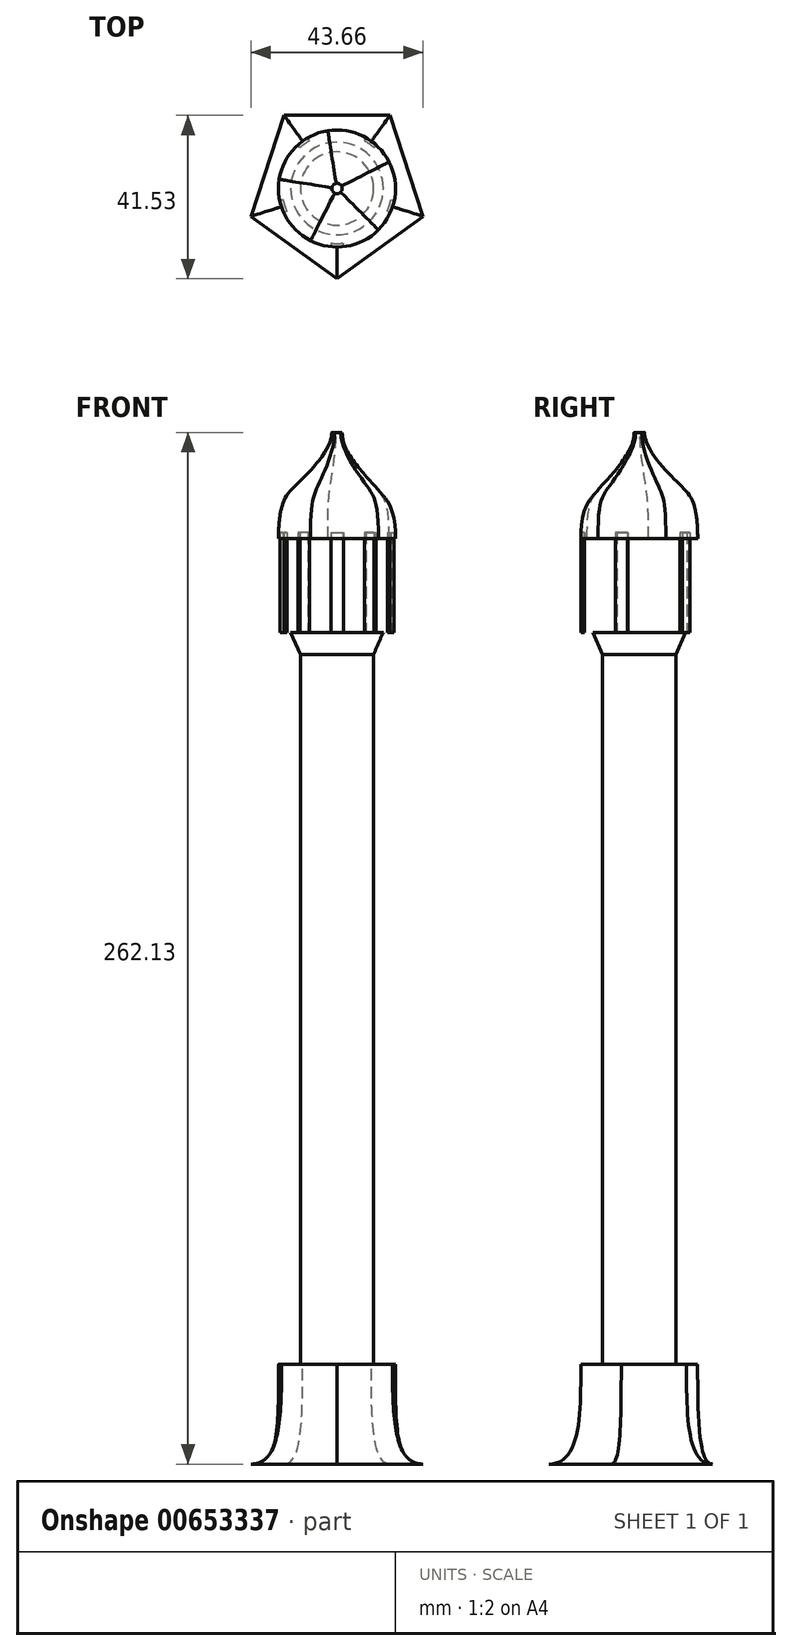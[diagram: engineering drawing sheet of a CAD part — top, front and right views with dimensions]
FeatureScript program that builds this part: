
annotation { "Feature Type Name" : "Feature", "Feature Type Description" : "" }
export const myFeature = defineFeature(function(context is Context, id is Id, definition is map)
    precondition{}
    {
        {
            var Q0;
            Q0=qCreatedBy(makeId("Top.planeOp"),FACE);
            var sketch = newSketch(context, id + "F0", { "sketchPlane" : qUnion([Q0])});
            skCircle(sketch, "E0.cCircle", {"center": v(0, 0) * mm, "radius": 18.57 * mm, "construction": true});
            skLineSegment(sketch, "E0.0", {"start": v(-13.5, 18.57) * mm, "end": v(13.5, 18.57) * mm});
            skLineSegment(sketch, "E0.1", {"start": v(13.5, 18.57) * mm, "end": v(21.83, -7.1) * mm});
            skLineSegment(sketch, "E0.2", {"start": v(21.83, -7.1) * mm, "end": v(0, -22.96) * mm});
            skLineSegment(sketch, "E0.3", {"start": v(0, -22.96) * mm, "end": v(-21.83, -7.1) * mm});
            skLineSegment(sketch, "E0.4", {"start": v(-21.83, -7.1) * mm, "end": v(-13.5, 18.57) * mm});
            skPoint(sketch, "E0.0.midPoint", {"position": v(0, 18.57) * mm});
            skSolve(sketch);
        }
        {
            var Q0;
            Q0=qCreatedBy(makeId("Top.planeOp"),FACE);
            cPlane(context, id + "F1", {"entities" : qUnion([Q0]), "cplaneType" : CPlaneType.OFFSET, "offset" : 25.4 * mm, "width" : 152.4 * mm, "height" : 152.4 * mm});
        }
        {
            var Q0;
            Q0=qCreatedBy(id+"F1.planeOp",FACE);
            var sketch = newSketch(context, id + "F2", { "sketchPlane" : qUnion([Q0])});
            skCircle(sketch, "E1", {"center": v(0, 0) * mm, "radius": 14.84 * mm});
            skSolve(sketch);
        }
        {
            var Q0;
            Q0 = qSketchRegion(id + "F0", true);
            var Q1;
            Q1 = qSketchRegion(id + "F2", true);
            loft(context, id + "F3", {"startCondition" : LoftEndDerivativeType.TANGENT_TO_PROFILE, "startMagnitude" : 3, "endCondition" : LoftEndDerivativeType.TANGENT_TO_PROFILE, "endMagnitude" : 0, "sheetProfilesArray" : [{ "sheetProfileEntities" : qUnion([Q0]) }, { "sheetProfileEntities" : qUnion([Q1]) }]});
        }
        {
            var Q0;
            Q0=makeQuery(id+"F3.opLoft","CAP_FACE",FACE,{"disambiguationData":[OSD([makeQuery(id+"F2.imprint","IMPRINT",FACE,{"disambiguationData":[TD([[makeQuery(id+"F2.imprint","IMPRINT",EDGE,{"derivedFrom":sQuery(id+"F2.wireOp",EDGE,"E1")}),1.0]])]})])],"isStart":true});
            var sketch = newSketch(context, id + "F4", { "sketchPlane" : qUnion([Q0])});
            skCircle(sketch, "E2", {"center": v(0, 0) * mm, "radius": 9.3 * mm});
            skSolve(sketch);
        }
        {
            var Q0;
            Q0 = qSketchRegion(id + "F4", true);
            extrude(context, id + "F5", {"entities" : qUnion([Q0]), "operationType" : NewBodyOperationType.ADD, "depth" : 180.34 * mm, "offsetDistance" : 25.4 * mm});
        }
        {
            var Q0;
            Q0=makeQuery(id+"F5.opExtrude","CAP_FACE",FACE,{"disambiguationData":[OSD([sQuery(id+"F4.wireOp",EDGE,"E2")])],"isStart":false});
            cPlane(context, id + "F6", {"entities" : qUnion([Q0]), "cplaneType" : CPlaneType.OFFSET, "offset" : 5.6 * mm, "width" : 152.4 * mm, "height" : 152.4 * mm});
        }
        {
            var Q0;
            Q0=qCreatedBy(id+"F6.planeOp",FACE);
            var sketch = newSketch(context, id + "F7", { "sketchPlane" : qUnion([Q0])});
            skCircle(sketch, "E3", {"center": v(0, 0) * mm, "radius": 11.76 * mm});
            skSolve(sketch);
        }
        {
            var Q1;
            Q1=makeQuery(id+"F7.imprint","IMPRINT",FACE,{"disambiguationData":[TD([[makeQuery(id+"F7.imprint","IMPRINT",EDGE,{"derivedFrom":sQuery(id+"F7.wireOp",EDGE,"E3")}),1.0]])]});
            var Q2;
            Q2=makeQuery(id+"F5.opExtrude","CAP_FACE",FACE,{"disambiguationData":[OSD([sQuery(id+"F4.wireOp",EDGE,"E2")])],"isStart":false});
            loft(context, id + "F8", {"operationType" : NewBodyOperationType.ADD, "sheetProfilesArray" : [{ "sheetProfileEntities" : qUnion([Q1]) }, { "sheetProfileEntities" : qUnion([Q2]) }]});
        }
        {
            var Q0;
            Q0=makeQuery(id+"F8.opLoft","CAP_FACE",FACE,{"disambiguationData":[OSD([makeQuery(id+"F7.imprint","IMPRINT",FACE,{"disambiguationData":[TD([[makeQuery(id+"F7.imprint","IMPRINT",EDGE,{"derivedFrom":sQuery(id+"F7.wireOp",EDGE,"E3")}),1.0]])]})])],"isStart":true});
            var sketch = newSketch(context, id + "F9", { "sketchPlane" : qUnion([Q0])});
            skArc(sketch, "E4", {"start": v(-6.97, 12.13) * mm, "mid": v(-8.24, 11.3) * mm, "end": v(-9.4, 10.36) * mm});
            skArc(sketch, "E5", {"start": v(-7.38, 12.83) * mm, "mid": v(-8.71, 11.96) * mm, "end": v(-9.95, 10.96) * mm});
            skLineSegment(sketch, "E6", {"start": v(6.95, 12.14) * mm, "end": v(7.35, 12.85) * mm});
            skLineSegment(sketch, "E7", {"start": v(9.38, 10.38) * mm, "end": v(9.92, 10.98) * mm});
            skLineSegment(sketch, "E8.1.0", {"start": v(-6.97, 12.13) * mm, "end": v(-7.38, 12.83) * mm});
            skLineSegment(sketch, "E8.1.1", {"start": v(-9.4, 10.36) * mm, "end": v(-9.95, 10.96) * mm});
            skLineSegment(sketch, "E8.2.0", {"start": v(-13.69, -2.89) * mm, "end": v(-14.48, -3.05) * mm});
            skLineSegment(sketch, "E8.2.1", {"start": v(-12.76, -5.74) * mm, "end": v(-13.5, -6.07) * mm});
            skLineSegment(sketch, "E8.3.0", {"start": v(-1.49, -13.91) * mm, "end": v(-1.57, -14.72) * mm});
            skLineSegment(sketch, "E8.3.1", {"start": v(1.52, -13.9) * mm, "end": v(1.6, -14.71) * mm});
            skLineSegment(sketch, "E8.4.0", {"start": v(12.77, -5.71) * mm, "end": v(13.51, -6.04) * mm});
            skLineSegment(sketch, "E8.4.1", {"start": v(13.7, -2.86) * mm, "end": v(14.49, -3.02) * mm});
            skArc(sketch, "E9.trimOffspring", {"start": v(9.38, 10.38) * mm, "mid": v(8.21, 11.33) * mm, "end": v(6.95, 12.14) * mm});
            skArc(sketch, "E10.trimOffspring", {"start": v(12.77, -5.71) * mm, "mid": v(13.3, -4.3) * mm, "end": v(13.7, -2.86) * mm});
            skArc(sketch, "E11.trimOffspring", {"start": v(13.51, -6.04) * mm, "mid": v(14.08, -4.56) * mm, "end": v(14.49, -3.02) * mm});
            skArc(sketch, "E12.trimOffspring", {"start": v(-14.48, -3.05) * mm, "mid": v(-14.07, -4.59) * mm, "end": v(-13.5, -6.07) * mm});
            skArc(sketch, "E13.trimOffspring", {"start": v(-13.69, -2.89) * mm, "mid": v(-13.3, -4.34) * mm, "end": v(-12.76, -5.74) * mm});
            skArc(sketch, "E14.trimOffspring", {"start": v(-1.57, -14.72) * mm, "mid": v(0.02, -14.8) * mm, "end": v(1.6, -14.71) * mm});
            skArc(sketch, "E15.trimOffspring", {"start": v(-1.49, -13.91) * mm, "mid": v(0.01, -14) * mm, "end": v(1.52, -13.9) * mm});
            skLineSegment(sketch, "E16", {"start": v(7.35, 12.85) * mm, "end": v(9.92, 10.98) * mm});
            skSolve(sketch);
        }
        {
            var Q0;
            Q0 = qSketchRegion(id + "F9", true);
            extrude(context, id + "F10", {"entities" : qUnion([Q0]), "depth" : 25.4 * mm, "offsetDistance" : 25.4 * mm});
        }
        {
            var Q0;
            Q0=makeQuery(id+"F10.opExtrude","CAP_FACE",FACE,{"disambiguationData":[OSD([sQuery(id+"F9.wireOp",EDGE,"E4"),sQuery(id+"F9.wireOp",EDGE,"E5"),sQuery(id+"F9.wireOp",EDGE,"E8.1.0"),sQuery(id+"F9.wireOp",EDGE,"E8.1.1")])],"isStart":false});
            cPlane(context, id + "F11", {"entities" : qUnion([Q0]), "cplaneType" : CPlaneType.OFFSET, "offset" : 12.2 * mm, "width" : 152.4 * mm, "height" : 152.4 * mm});
        }
        {
            var Q0;
            Q0=makeQuery(id+"F10.opExtrude","CAP_FACE",FACE,{"disambiguationData":[OSD([sQuery(id+"F9.wireOp",EDGE,"E8.4.0"),sQuery(id+"F9.wireOp",EDGE,"E8.4.1"),sQuery(id+"F9.wireOp",EDGE,"E10.trimOffspring"),sQuery(id+"F9.wireOp",EDGE,"E11.trimOffspring")])],"isStart":false});
            cPlane(context, id + "F12", {"entities" : qUnion([Q0]), "cplaneType" : CPlaneType.OFFSET, "offset" : 25.4 * mm, "width" : 152.4 * mm, "height" : 152.4 * mm});
        }
        {
            var Q0;
            Q0=qCreatedBy(id+"F11.planeOp",FACE);
            var sketch = newSketch(context, id + "F13", { "sketchPlane" : qUnion([Q0])});
            skCircle(sketch, "E17", {"center": v(0, 0) * mm, "radius": 8.38 * mm, "construction": true});
            skLineSegment(sketch, "E18.0", {"start": v(-1.63, 10.23) * mm, "end": v(9.23, 4.7) * mm});
            skLineSegment(sketch, "E18.1", {"start": v(9.23, 4.7) * mm, "end": v(7.33, -7.32) * mm});
            skLineSegment(sketch, "E18.2", {"start": v(7.33, -7.32) * mm, "end": v(-4.7, -9.23) * mm});
            skLineSegment(sketch, "E18.3", {"start": v(-4.7, -9.23) * mm, "end": v(-10.23, 1.62) * mm});
            skLineSegment(sketch, "E18.4", {"start": v(-10.23, 1.62) * mm, "end": v(-1.63, 10.23) * mm});
            skPoint(sketch, "E18.0.midPoint", {"position": v(3.8, 7.47) * mm});
            skSolve(sketch);
        }
        {
            var Q0;
            Q0=qCreatedBy(id+"F12.planeOp",FACE);
            var sketch = newSketch(context, id + "F14", { "sketchPlane" : qUnion([Q0])});
            skCircle(sketch, "E19", {"center": v(0, 0) * mm, "radius": 1.32 * mm});
            skSolve(sketch);
        }
        {
            var Q0;
            Q0=makeQuery(id+"F8.opLoft","CAP_FACE",FACE,{"disambiguationData":[OSD([makeQuery(id+"F7.imprint","IMPRINT",FACE,{"disambiguationData":[TD([[makeQuery(id+"F7.imprint","IMPRINT",EDGE,{"derivedFrom":sQuery(id+"F7.wireOp",EDGE,"E3")}),1.0]])]})])],"isStart":true});
            cPlane(context, id + "F15", {"entities" : qUnion([Q0]), "cplaneType" : CPlaneType.OFFSET, "offset" : 23.88 * mm, "width" : 152.4 * mm, "height" : 152.4 * mm});
        }
        {
            var Q0;
            Q0=qCreatedBy(id+"F15.planeOp",FACE);
            var sketch = newSketch(context, id + "F16", { "sketchPlane" : qUnion([Q0])});
            skCircle(sketch, "E20", {"center": v(0, 0) * mm, "radius": 14.86 * mm});
            skSolve(sketch);
        }
        {
            var Q0;
            Q0=makeQuery(id+"F16.imprint","IMPRINT",FACE,{"disambiguationData":[TD([[makeQuery(id+"F16.imprint","IMPRINT",EDGE,{"derivedFrom":sQuery(id+"F16.wireOp",EDGE,"E20")}),1.0]])]});
            var Q1;
            Q1=makeQuery(id+"F13.imprint","IMPRINT",FACE,{"disambiguationData":[TD([[makeQuery(id+"F13.imprint","IMPRINT",EDGE,{"derivedFrom":sQuery(id+"F13.wireOp",EDGE,"E18.0")}),-1.0]])]});
            var Q2;
            Q2=makeQuery(id+"F14.imprint","IMPRINT",FACE,{"disambiguationData":[TD([[makeQuery(id+"F14.imprint","IMPRINT",EDGE,{"derivedFrom":sQuery(id+"F14.wireOp",EDGE,"E19")}),1.0]])]});
            loft(context, id + "F17", {"startCondition" : LoftEndDerivativeType.NORMAL_TO_PROFILE, "startMagnitude" : 2, "endCondition" : LoftEndDerivativeType.NORMAL_TO_PROFILE, "endMagnitude" : 1, "sheetProfilesArray" : [{ "sheetProfileEntities" : qUnion([Q0]) }, { "sheetProfileEntities" : qUnion([Q1]) }, { "sheetProfileEntities" : qUnion([Q2]) }]});
        }
    });
